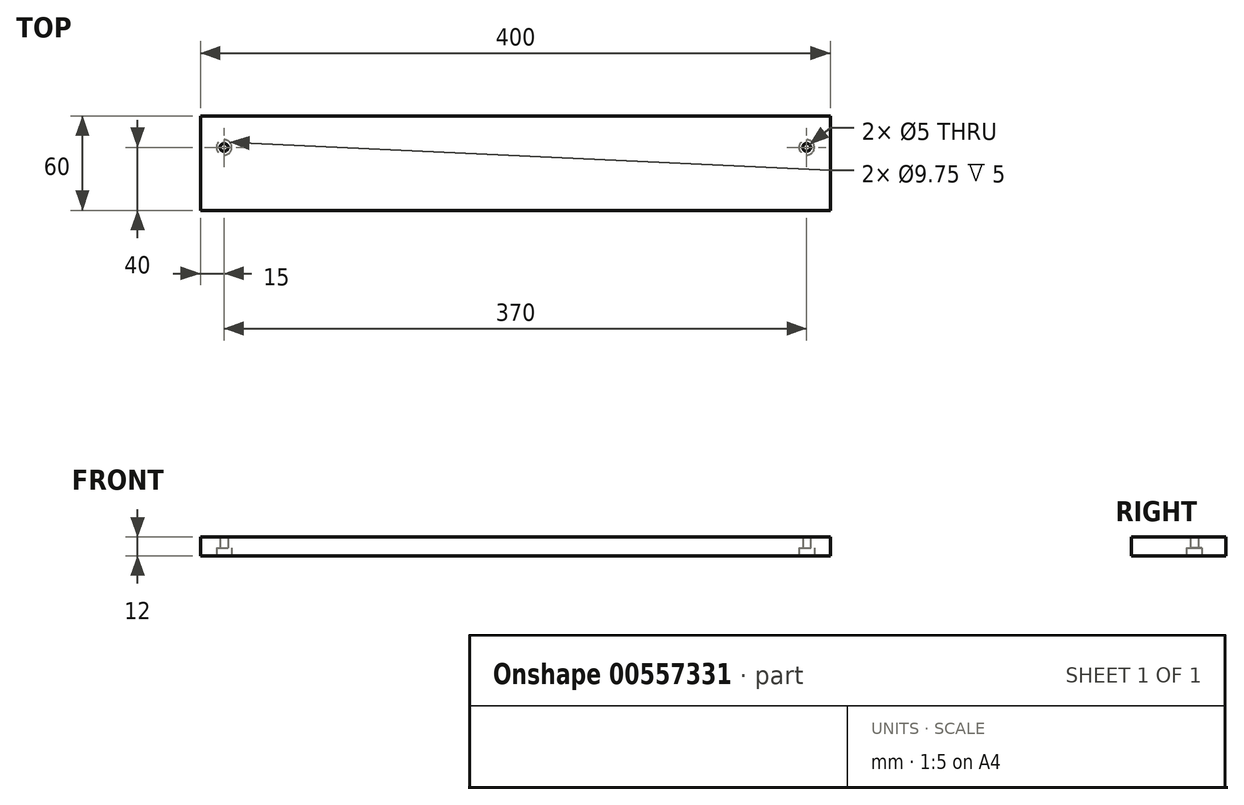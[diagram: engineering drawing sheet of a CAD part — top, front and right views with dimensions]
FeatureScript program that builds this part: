
annotation { "Feature Type Name" : "Feature", "Feature Type Description" : "" }
export const myFeature = defineFeature(function(context is Context, id is Id, definition is map)
    precondition{}
    {
        {
            var Q0;
            Q0=qCreatedBy(makeId("Top.planeOp"),FACE);
            var sketch = newSketch(context, id + "F0", { "sketchPlane" : qUnion([Q0])});
            skLineSegment(sketch, "E0.bottom", {"start": v(0, 0) * mm, "end": v(400, 0) * mm});
            skLineSegment(sketch, "E0.top", {"start": v(0, -60) * mm, "end": v(400, -60) * mm});
            skLineSegment(sketch, "E0.left", {"start": v(0, 0) * mm, "end": v(0, -60) * mm});
            skLineSegment(sketch, "E0.right", {"start": v(400, 0) * mm, "end": v(400, -60) * mm});
            skSolve(sketch);
        }
        {
            var Q0;
            Q0 = qSketchRegion(id + "F0", true);
            extrude(context, id + "F1", {"entities" : qUnion([Q0]), "depth" : 12 * mm, "offsetDistance" : 25 * mm});
        }
        {
            var Q0;
            Q0=makeQuery(id+"F1.opExtrude","CAP_FACE",FACE,{"disambiguationData":[OSD([sQuery(id+"F0.wireOp",EDGE,"E0.bottom"),sQuery(id+"F0.wireOp",EDGE,"E0.top"),sQuery(id+"F0.wireOp",EDGE,"E0.left"),sQuery(id+"F0.wireOp",EDGE,"E0.right")])],"isStart":true});
            var sketch = newSketch(context, id + "F2", { "sketchPlane" : qUnion([Q0])});
            skCircle(sketch, "E1", {"center": v(15, 20) * mm, "radius": 2.5 * mm});
            skCircle(sketch, "E2", {"center": v(385, 20) * mm, "radius": 2.5 * mm});
            skSolve(sketch);
        }
        {
            var Q0;
            Q0=sQuery(id+"F2.wireOp",VERTEX,"E1.center");
            var Q1;
            Q1=sQuery(id+"F2.wireOp",VERTEX,"E2.center");
            var Q2;
            Q2=makeQuery(id+"F1.opExtrude","SWEPT_BODY",BODY,{"disambiguationData":[OSD([sQuery(id+"F0.wireOp",EDGE,"E0.bottom"),sQuery(id+"F0.wireOp",EDGE,"E0.top"),sQuery(id+"F0.wireOp",EDGE,"E0.left"),sQuery(id+"F0.wireOp",EDGE,"E0.right")])]});
            hole(context, id + "F3", {"style" : HoleStyle.C_BORE, "endStyle" : HoleEndStyle.THROUGH, "holeDiameter" : 5 * mm, "cBoreDiameter" : 9.75 * mm, "cBoreDepth" : 5 * mm, "majorDiameter" : 5 * mm, "isTappedThrough" : true, "tappedDepth" : 13.5 * mm, "tapClearance" : 3, "locations" : qUnion([Q0, Q1]), "scope" : qUnion([Q2])});
        }
    });
